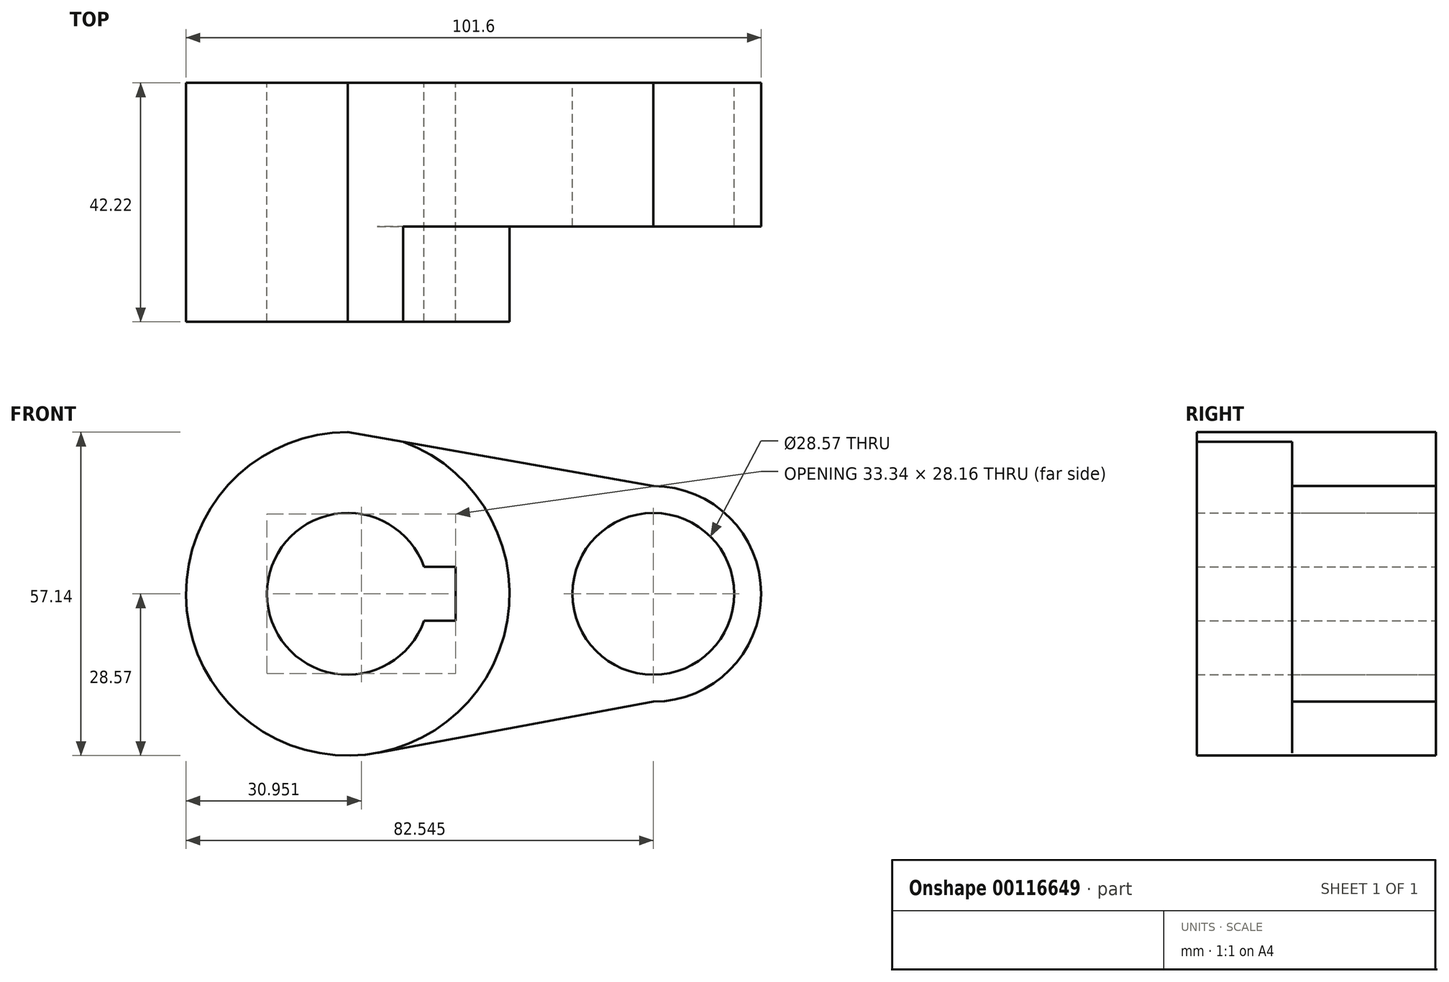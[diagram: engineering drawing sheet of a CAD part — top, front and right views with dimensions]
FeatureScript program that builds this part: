
annotation { "Feature Type Name" : "Feature", "Feature Type Description" : "" }
export const myFeature = defineFeature(function(context is Context, id is Id, definition is map)
    precondition{}
    {
        {
            var Q0;
            Q0=qCreatedBy(makeId("Front.planeOp"),FACE);
            var sketch = newSketch(context, id + "F0", { "sketchPlane" : qUnion([Q0])});
            skCircle(sketch, "E0", {"center": v(0, 0) * mm, "radius": 28.57 * mm});
            skCircle(sketch, "E1", {"center": v(53.98, 0) * mm, "radius": 19.05 * mm});
            skLineSegment(sketch, "E2", {"start": v(0, 28.58) * mm, "end": v(53.98, 19.05) * mm});
            skLineSegment(sketch, "E3", {"start": v(53.98, -19.05) * mm, "end": v(0, -29.06) * mm});
            skCircle(sketch, "E4", {"center": v(0, 0) * mm, "radius": 14.29 * mm});
            skCircle(sketch, "E5", {"center": v(53.98, 0) * mm, "radius": 14.29 * mm});
            skLineSegment(sketch, "E6.bottom", {"start": v(19.05, 4.76) * mm, "end": v(-19.05, 4.76) * mm});
            skLineSegment(sketch, "E6.top", {"start": v(19.05, -4.76) * mm, "end": v(-19.05, -4.76) * mm});
            skLineSegment(sketch, "E6.left", {"start": v(19.05, 4.76) * mm, "end": v(19.05, -4.76) * mm});
            skLineSegment(sketch, "E6.right", {"start": v(-19.05, 4.76) * mm, "end": v(-19.05, -4.76) * mm});
            skSolve(sketch);
        }
        {
            var Q0;
            {var subQ0=sQuery(id+"F0.wireOp",EDGE,"E6.left");Q0=makeQuery(id+"F0.imprint","IMPRINT",FACE,{"disambiguationData":[TD([[makeQuery(id+"F0.imprint","IMPRINT",EDGE,{"derivedFrom":subQ0}),1.0]])]});}
            var Q1;
            {var subQ0=sQuery(id+"F0.wireOp",EDGE,"E3");var subQ1=sQuery(id+"F0.wireOp",EDGE,"E0");var subQ2=makeQuery(id+"F0.imprint","INTERSECT",VERTEX,{"derivedFrom":[subQ1,subQ0]});Q1=makeQuery(id+"F0.imprint","IMPRINT",FACE,{"disambiguationData":[TD([[makeQuery(id+"F0.imprint","IMPRINT",EDGE,{"disambiguationData":[TD([[subQ2,-1.0]])],"derivedFrom":subQ1}),-1.0]])]});}
            var Q2;
            Q2=makeQuery(id+"F0.imprint","IMPRINT",FACE,{"disambiguationData":[TD([[makeQuery(id+"F0.imprint","IMPRINT",EDGE,{"derivedFrom":sQuery(id+"F0.wireOp",EDGE,"E5")}),-1.0]])]});
            var Q3;
            {var subQ5=sQuery(id+"F0.wireOp",EDGE,"E6.right");Q3=makeQuery(id+"F0.imprint","IMPRINT",FACE,{"disambiguationData":[TD([[makeQuery(id+"F0.imprint","IMPRINT",EDGE,{"derivedFrom":subQ5}),1.0]])]});}
            extrude(context, id + "F1", {"entities" : qUnion([Q0, Q1, Q2, Q3]), "depth" : 25.4 * mm});
        }
        {
            var Q0;
            {var subQ0=sQuery(id+"F0.wireOp",EDGE,"E6.left");Q0=makeQuery(id+"F0.imprint","IMPRINT",FACE,{"disambiguationData":[TD([[makeQuery(id+"F0.imprint","IMPRINT",EDGE,{"derivedFrom":subQ0}),1.0]])]});}
            var Q1;
            {var subQ5=sQuery(id+"F0.wireOp",EDGE,"E6.right");Q1=makeQuery(id+"F0.imprint","IMPRINT",FACE,{"disambiguationData":[TD([[makeQuery(id+"F0.imprint","IMPRINT",EDGE,{"derivedFrom":subQ5}),1.0]])]});}
            extrude(context, id + "F2", {"entities" : qUnion([Q0, Q1]), "operationType" : NewBodyOperationType.ADD, "depth" : 42.22 * mm});
        }
    });
